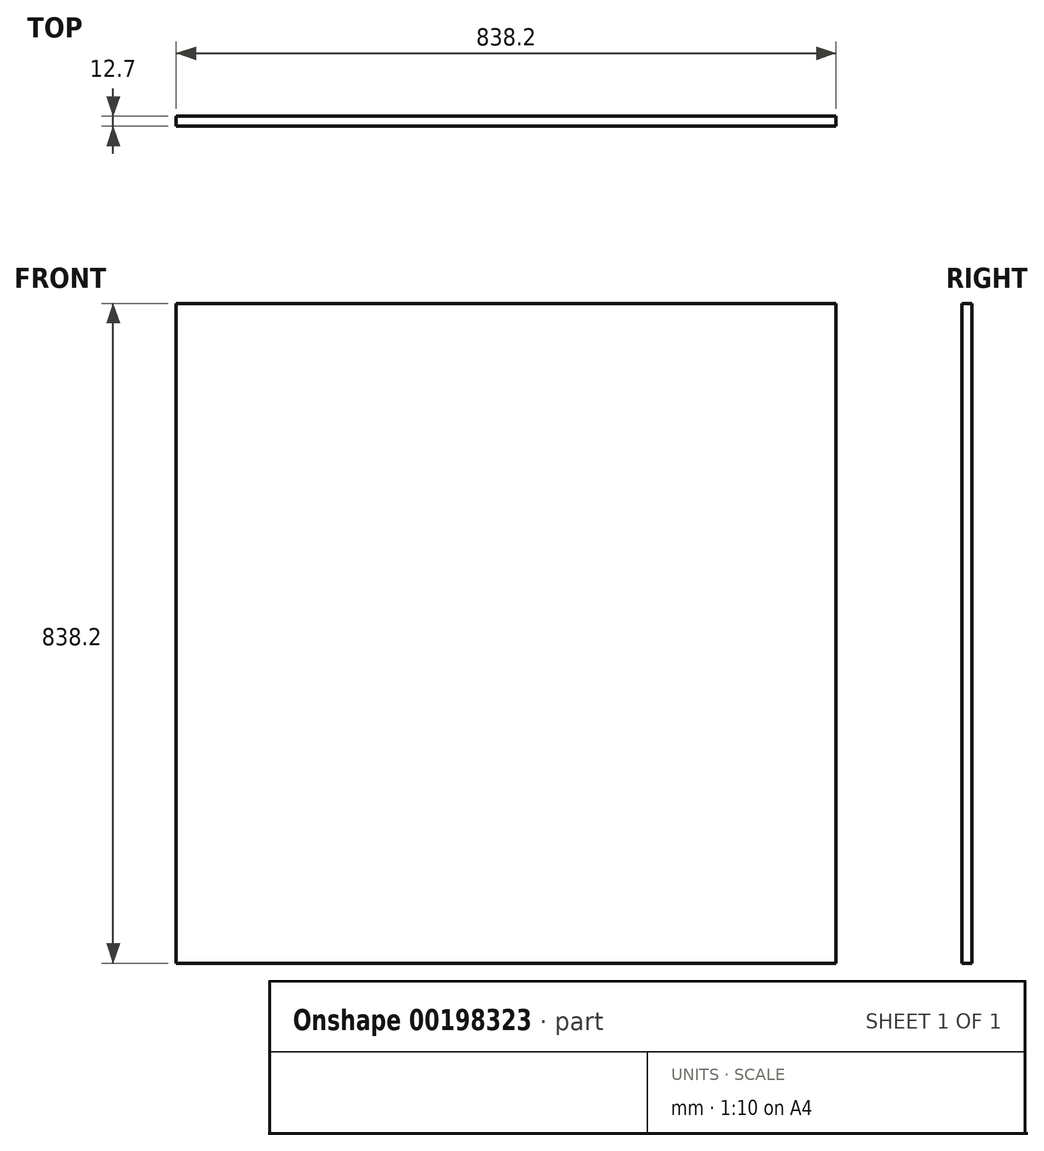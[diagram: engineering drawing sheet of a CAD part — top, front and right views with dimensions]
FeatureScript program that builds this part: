
annotation { "Feature Type Name" : "Feature", "Feature Type Description" : "" }
export const myFeature = defineFeature(function(context is Context, id is Id, definition is map)
    precondition{}
    {
        {
            var Q0;
            Q0=qCreatedBy(makeId("Front.planeOp"),FACE);
            var sketch = newSketch(context, id + "F0", { "sketchPlane" : qUnion([Q0])});
            skLineSegment(sketch, "E0.bottom", {"start": v(-420.52, 490.9) * mm, "end": v(417.68, 490.9) * mm});
            skLineSegment(sketch, "E0.top", {"start": v(-420.52, -347.3) * mm, "end": v(417.68, -347.3) * mm});
            skLineSegment(sketch, "E0.left", {"start": v(-420.52, 490.9) * mm, "end": v(-420.52, -347.3) * mm});
            skLineSegment(sketch, "E0.right", {"start": v(417.68, 490.9) * mm, "end": v(417.68, -347.3) * mm});
            skSolve(sketch);
        }
        {
            var Q0;
            Q0=sQuery(id+"F0.wireOp",EDGE,"E0.bottom");
            var Q1;
            Q1=sQuery(id+"F0.wireOp",EDGE,"E0.right");
            var Q2;
            Q2=sQuery(id+"F0.wireOp",EDGE,"E0.top");
            var Q3;
            Q3=sQuery(id+"F0.wireOp",EDGE,"E0.left");
            extrude(context, id + "F1", {"bodyType" : ToolBodyType.SURFACE, "surfaceEntities" : qUnion([Q0, Q1, Q2, Q3]), "depth" : 12.7 * mm});
        }
    });
